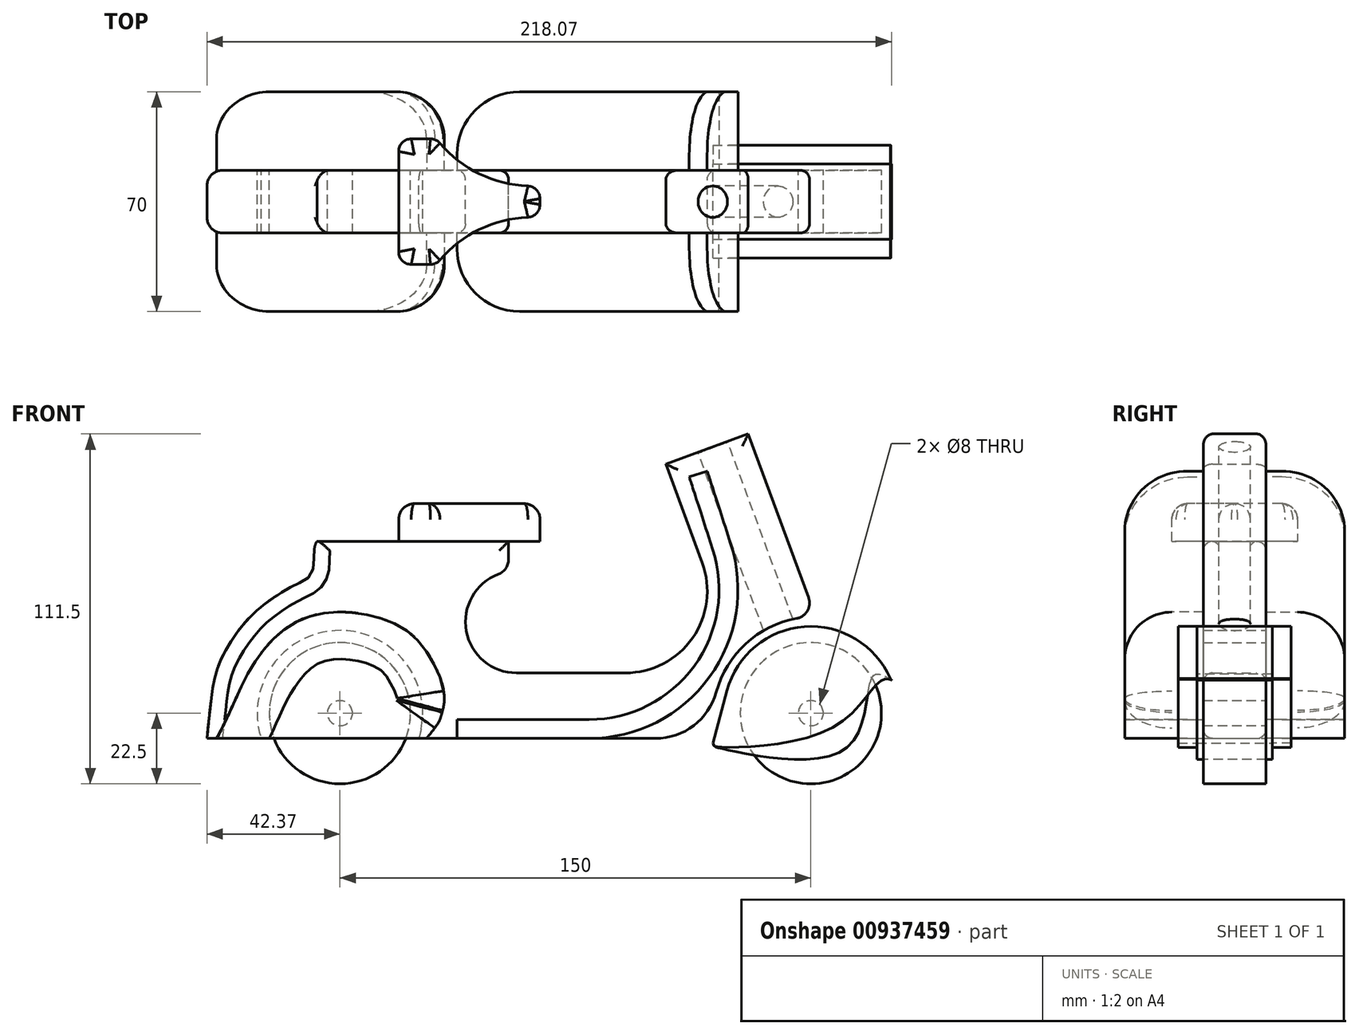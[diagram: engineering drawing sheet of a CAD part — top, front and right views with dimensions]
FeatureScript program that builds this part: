
annotation { "Feature Type Name" : "Feature", "Feature Type Description" : "" }
export const myFeature = defineFeature(function(context is Context, id is Id, definition is map)
    precondition{}
    {
        {
            var Q0;
            Q0=qCreatedBy(makeId("Front.planeOp"),FACE);
            var sketch = newSketch(context, id + "F0", { "sketchPlane" : qUnion([Q0])});
            skCircle(sketch, "E0", {"center": v(0, 0) * mm, "radius": 4 * mm, "construction": true});
            skCircle(sketch, "E1", {"center": v(0, 0) * mm, "radius": 22.5 * mm, "construction": true});
            skCircle(sketch, "E2", {"center": v(-150, 0) * mm, "radius": 4 * mm, "construction": true});
            skCircle(sketch, "E3", {"center": v(-150, 0) * mm, "radius": 22.5 * mm, "construction": true});
            skArc(sketch, "E4", {"start": v(1.52, 30.72) * mm, "mid": v(-23.75, 18.96) * mm, "end": v(-30.7, -8.03) * mm});
            skLineSegment(sketch, "E5", {"start": v(0, 0) * mm, "end": v(-39.23, 106.54) * mm, "construction": true});
            skArc(sketch, "E6", {"start": v(-124.9, -8.03) * mm, "mid": v(-150, 26.35) * mm, "end": v(-175.1, -8.03) * mm});
            skLineSegment(sketch, "E7", {"start": v(-30.7, -8.03) * mm, "end": v(-124.9, -8.03) * mm});
            skFitSpline(sketch, "E8", {"points": [v(-192.37, -8.03) * mm, v(-189.97, 10.9) * mm, v(-185.76, 21.1) * mm, v(-177.35, 31.92) * mm, v(-164.13, 40.93) * mm, v(-158.73, 45.14) * mm, v(-157.32, 54.76) * mm], "startDerivative": vector(9.9, 79.49) * mm, "endDerivative": vector(32.15, 42.3) * mm});
            skLineSegment(sketch, "E9", {"start": v(-157.32, 54.76) * mm, "end": v(-96.28, 54.76) * mm});
            skLineSegment(sketch, "E10", {"start": v(-96.28, 54.76) * mm, "end": v(-96.28, 45.15) * mm});
            skArc(sketch, "E11", {"start": v(-96.28, 45.15) * mm, "mid": v(-109.96, 27.81) * mm, "end": v(-93.75, 12.82) * mm});
            skLineSegment(sketch, "E12", {"start": v(-93.75, 12.82) * mm, "end": v(-59.07, 12.82) * mm});
            skArc(sketch, "E13", {"start": v(-59.07, 12.82) * mm, "mid": v(-37.68, 23.98) * mm, "end": v(-34.6, 47.9) * mm});
            skLineSegment(sketch, "E14", {"start": v(-34.6, 47.9) * mm, "end": v(-46.17, 79.34) * mm});
            skLineSegment(sketch, "E15", {"start": v(-46.17, 79.34) * mm, "end": v(-19.94, 89) * mm});
            skLineSegment(sketch, "E16", {"start": v(-19.94, 89) * mm, "end": v(1.52, 30.72) * mm});
            skLineSegment(sketch, "E17.trimOffspring", {"start": v(-175.1, -8.03) * mm, "end": v(-192.37, -8.03) * mm});
            skSolve(sketch);
        }
        {
            var Q0;
            Q0=makeQuery(id+"F0.imprint","IMPRINT",FACE,{"disambiguationData":[TD([[makeQuery(id+"F0.imprint","IMPRINT",EDGE,{"derivedFrom":sQuery(id+"F0.wireOp",EDGE,"E4")}),-1.0]])]});
            var Q1;
            Q1=sQuery(id+"F0.wireOp",EDGE,"E3");
            var Q2;
            Q2=sQuery(id+"F0.wireOp",EDGE,"E2");
            var Q3;
            Q3=sQuery(id+"F0.wireOp",EDGE,"E1");
            var Q4;
            Q4=sQuery(id+"F0.wireOp",EDGE,"E0");
            extrude(context, id + "F1", {"entities" : qUnion([Q0]), "surfaceEntities" : qUnion([Q1, Q2, Q3, Q4]), "depth" : 10 * mm, "offsetDistance" : 25 * mm, "hasSecondDirection" : true, "secondDirectionOppositeDirection" : true, "secondDirectionDepth" : 10 * mm});
        }
        {
            var Q0;
            Q0=makeQuery(id+"F1.opExtrude","SWEPT_FACE",FACE,{"disambiguationData":[OSD([sQuery(id+"F0.wireOp",EDGE,"E15")])]});
            var sketch = newSketch(context, id + "F2", { "sketchPlane" : qUnion([Q0])});
            skCircle(sketch, "E18", {"center": v(0, 0) * mm, "radius": 5 * mm});
            skSolve(sketch);
        }
        {
            var Q0;
            Q0 = qSketchRegion(id + "F2", true);
            extrude(context, id + "F3", {"entities" : qUnion([Q0]), "operationType" : NewBodyOperationType.REMOVE, "endBound" : BoundingType.THROUGH_ALL, "oppositeDirection" : true, "depth" : 25 * mm, "offsetDistance" : 25 * mm});
        }
        {
            var Q0;
            Q0=makeQuery(id+"F1.opExtrude","SWEPT_EDGE",EDGE,{"disambiguationData":[OSD([sQuery(id+"F0.wireOp",EDGE,"E4"),sQuery(id+"F0.wireOp",EDGE,"E16")])]});
            var Q1;
            Q1=makeQuery(id+"F1.opExtrude","SWEPT_EDGE",EDGE,{"disambiguationData":[OSD([sQuery(id+"F0.wireOp",EDGE,"E10"),sQuery(id+"F0.wireOp",EDGE,"E11")])]});
            fillet(context, id + "F4", {"entities" : qUnion([Q0, Q1]), "radius" : 5 * mm, "tangentPropagation" : true, "allowEdgeOverflow" : false});
        }
        {
            var Q0;
            Q0=makeQuery(id+"F1.opExtrude","SWEPT_EDGE",EDGE,{"disambiguationData":[OSD([sQuery(id+"F0.wireOp",EDGE,"E4"),sQuery(id+"F0.wireOp",EDGE,"E7")])]});
            fillet(context, id + "F5", {"entities" : qUnion([Q0]), "radius" : 20 * mm, "tangentPropagation" : true, "allowEdgeOverflow" : false});
        }
        {
            var Q0;
            Q0=makeQuery(id+"F1.opExtrude","CAP_EDGE",EDGE,{"disambiguationData":[OSD([sQuery(id+"F0.wireOp",EDGE,"E9")])],"isStart":true});
            var Q1;
            {var subQ0=sQuery(id+"F0.wireOp",EDGE,"E11");var subQ1=sQuery(id+"F0.wireOp",EDGE,"E10");Q1=makeQuery(id+"F4.opFillet","BLEND_EDGE",EDGE,{"blendedFrom":[makeQuery(id+"F1.opExtrude","SWEPT_EDGE",EDGE,{"disambiguationData":[OSD([subQ1,subQ0])]}),makeQuery(id+"F1.opExtrude","CAP_FACE",FACE,{"disambiguationData":[OSD([sQuery(id+"F0.wireOp",EDGE,"E4"),sQuery(id+"F0.wireOp",EDGE,"E6"),sQuery(id+"F0.wireOp",EDGE,"E7"),sQuery(id+"F0.wireOp",EDGE,"E8"),sQuery(id+"F0.wireOp",EDGE,"E9"),subQ1,subQ0,sQuery(id+"F0.wireOp",EDGE,"E12"),sQuery(id+"F0.wireOp",EDGE,"E13"),sQuery(id+"F0.wireOp",EDGE,"E14"),sQuery(id+"F0.wireOp",EDGE,"E15"),sQuery(id+"F0.wireOp",EDGE,"E16"),sQuery(id+"F0.wireOp",EDGE,"E17.trimOffspring")])],"isStart":true})],"blendedInto":[makeQuery(id+"F1.opExtrude","CAP_FACE",FACE,{"disambiguationData":[OSD([sQuery(id+"F0.wireOp",EDGE,"E4"),sQuery(id+"F0.wireOp",EDGE,"E6"),sQuery(id+"F0.wireOp",EDGE,"E7"),sQuery(id+"F0.wireOp",EDGE,"E8"),sQuery(id+"F0.wireOp",EDGE,"E9"),subQ1,subQ0,sQuery(id+"F0.wireOp",EDGE,"E12"),sQuery(id+"F0.wireOp",EDGE,"E13"),sQuery(id+"F0.wireOp",EDGE,"E14"),sQuery(id+"F0.wireOp",EDGE,"E15"),sQuery(id+"F0.wireOp",EDGE,"E16"),sQuery(id+"F0.wireOp",EDGE,"E17.trimOffspring")])],"isStart":true})]});}
            var Q2;
            Q2=makeQuery(id+"F1.opExtrude","CAP_EDGE",EDGE,{"disambiguationData":[OSD([sQuery(id+"F0.wireOp",EDGE,"E12")])],"isStart":true});
            var Q3;
            Q3=makeQuery(id+"F1.opExtrude","CAP_EDGE",EDGE,{"disambiguationData":[OSD([sQuery(id+"F0.wireOp",EDGE,"E13")])],"isStart":true});
            var Q4;
            Q4=makeQuery(id+"F1.opExtrude","CAP_EDGE",EDGE,{"disambiguationData":[OSD([sQuery(id+"F0.wireOp",EDGE,"E15")])],"isStart":true});
            var Q5;
            Q5=makeQuery(id+"F1.opExtrude","CAP_EDGE",EDGE,{"disambiguationData":[OSD([sQuery(id+"F0.wireOp",EDGE,"E16")])],"isStart":true});
            var Q6;
            Q6=makeQuery(id+"F1.opExtrude","CAP_EDGE",EDGE,{"disambiguationData":[OSD([sQuery(id+"F0.wireOp",EDGE,"E16")])],"isStart":false});
            var Q7;
            Q7=makeQuery(id+"F1.opExtrude","CAP_EDGE",EDGE,{"disambiguationData":[OSD([sQuery(id+"F0.wireOp",EDGE,"E15")])],"isStart":false});
            var Q8;
            Q8=makeQuery(id+"F1.opExtrude","CAP_EDGE",EDGE,{"disambiguationData":[OSD([sQuery(id+"F0.wireOp",EDGE,"E14")])],"isStart":false});
            var Q9;
            Q9=makeQuery(id+"F1.opExtrude","CAP_EDGE",EDGE,{"disambiguationData":[OSD([sQuery(id+"F0.wireOp",EDGE,"E13")])],"isStart":false});
            var Q10;
            Q10=makeQuery(id+"F1.opExtrude","CAP_EDGE",EDGE,{"disambiguationData":[OSD([sQuery(id+"F0.wireOp",EDGE,"E12")])],"isStart":false});
            var Q11;
            Q11=makeQuery(id+"F1.opExtrude","CAP_EDGE",EDGE,{"disambiguationData":[OSD([sQuery(id+"F0.wireOp",EDGE,"E11")])],"isStart":false});
            var Q12;
            {var subQ0=sQuery(id+"F0.wireOp",EDGE,"E11");var subQ1=sQuery(id+"F0.wireOp",EDGE,"E10");Q12=makeQuery(id+"F4.opFillet","BLEND_EDGE",EDGE,{"blendedFrom":[makeQuery(id+"F1.opExtrude","SWEPT_EDGE",EDGE,{"disambiguationData":[OSD([subQ1,subQ0])]}),makeQuery(id+"F1.opExtrude","CAP_FACE",FACE,{"disambiguationData":[OSD([sQuery(id+"F0.wireOp",EDGE,"E4"),sQuery(id+"F0.wireOp",EDGE,"E6"),sQuery(id+"F0.wireOp",EDGE,"E7"),sQuery(id+"F0.wireOp",EDGE,"E8"),sQuery(id+"F0.wireOp",EDGE,"E9"),subQ1,subQ0,sQuery(id+"F0.wireOp",EDGE,"E12"),sQuery(id+"F0.wireOp",EDGE,"E13"),sQuery(id+"F0.wireOp",EDGE,"E14"),sQuery(id+"F0.wireOp",EDGE,"E15"),sQuery(id+"F0.wireOp",EDGE,"E16"),sQuery(id+"F0.wireOp",EDGE,"E17.trimOffspring")])],"isStart":false})],"blendedInto":[makeQuery(id+"F1.opExtrude","CAP_FACE",FACE,{"disambiguationData":[OSD([sQuery(id+"F0.wireOp",EDGE,"E4"),sQuery(id+"F0.wireOp",EDGE,"E6"),sQuery(id+"F0.wireOp",EDGE,"E7"),sQuery(id+"F0.wireOp",EDGE,"E8"),sQuery(id+"F0.wireOp",EDGE,"E9"),subQ1,subQ0,sQuery(id+"F0.wireOp",EDGE,"E12"),sQuery(id+"F0.wireOp",EDGE,"E13"),sQuery(id+"F0.wireOp",EDGE,"E14"),sQuery(id+"F0.wireOp",EDGE,"E15"),sQuery(id+"F0.wireOp",EDGE,"E16"),sQuery(id+"F0.wireOp",EDGE,"E17.trimOffspring")])],"isStart":false})]});}
            var Q13;
            Q13=makeQuery(id+"F1.opExtrude","CAP_EDGE",EDGE,{"disambiguationData":[OSD([sQuery(id+"F0.wireOp",EDGE,"E9")])],"isStart":false});
            var Q14;
            Q14=makeQuery(id+"F1.opExtrude","CAP_EDGE",EDGE,{"disambiguationData":[OSD([sQuery(id+"F0.wireOp",EDGE,"E14")])],"isStart":true});
            var Q15;
            Q15=makeQuery(id+"F1.opExtrude","CAP_EDGE",EDGE,{"disambiguationData":[OSD([sQuery(id+"F0.wireOp",EDGE,"E11")])],"isStart":true});
            var Q16;
            Q16=makeQuery(id+"F1.opExtrude","CAP_EDGE",EDGE,{"disambiguationData":[OSD([sQuery(id+"F0.wireOp",EDGE,"E10")])],"isStart":false});
            var Q17;
            Q17=makeQuery(id+"F1.opExtrude","CAP_EDGE",EDGE,{"disambiguationData":[OSD([sQuery(id+"F0.wireOp",EDGE,"E10")])],"isStart":true});
            fillet(context, id + "F6", {"entities" : qUnion([Q0, Q1, Q2, Q3, Q4, Q5, Q6, Q7, Q8, Q9, Q10, Q11, Q12, Q13, Q14, Q15, Q16, Q17]), "radius" : 3 * mm, "tangentPropagation" : true, "allowEdgeOverflow" : false});
        }
        {
            var Q0;
            Q0=qCreatedBy(makeId("Front.planeOp"),FACE);
            var sketch = newSketch(context, id + "F7", { "sketchPlane" : qUnion([Q0])});
            skCircle(sketch, "E19.0", {"center": v(-150, 0) * mm, "radius": 22.5 * mm});
            skCircle(sketch, "E20.0", {"center": v(-150, 0) * mm, "radius": 4 * mm});
            skCircle(sketch, "E21.0", {"center": v(0, 0) * mm, "radius": 22.5 * mm});
            skCircle(sketch, "E22.0", {"center": v(0, 0) * mm, "radius": 4 * mm});
            skSolve(sketch);
        }
        {
            var Q0;
            Q0 = qSketchRegion(id + "F7", true);
            extrude(context, id + "F8", {"entities" : qUnion([Q0]), "depth" : 10 * mm, "offsetDistance" : 25 * mm, "hasSecondDirection" : true, "secondDirectionOppositeDirection" : true, "secondDirectionDepth" : 10 * mm});
        }
        {
            var Q0;
            Q0=makeQuery(id+"F1.opExtrude","CAP_FACE",FACE,{"disambiguationData":[OSD([sQuery(id+"F0.wireOp",EDGE,"E4"),sQuery(id+"F0.wireOp",EDGE,"E6"),sQuery(id+"F0.wireOp",EDGE,"E7"),sQuery(id+"F0.wireOp",EDGE,"E8"),sQuery(id+"F0.wireOp",EDGE,"E9"),sQuery(id+"F0.wireOp",EDGE,"E10"),sQuery(id+"F0.wireOp",EDGE,"E11"),sQuery(id+"F0.wireOp",EDGE,"E12"),sQuery(id+"F0.wireOp",EDGE,"E13"),sQuery(id+"F0.wireOp",EDGE,"E14"),sQuery(id+"F0.wireOp",EDGE,"E15"),sQuery(id+"F0.wireOp",EDGE,"E16"),sQuery(id+"F0.wireOp",EDGE,"E17.trimOffspring")])],"isStart":false});
            var sketch = newSketch(context, id + "F9", { "sketchPlane" : qUnion([Q0])});
            skLineSegment(sketch, "E23", {"start": v(-189.27, -8.03) * mm, "end": v(-122.4, -8.03) * mm});
            skFitSpline(sketch, "E24", {"points": [v(-122.4, -8.03) * mm, v(-118.5, -2.76) * mm, v(-117.52, 0) * mm, v(-116.74, 4.25) * mm, v(-117.77, 10.42) * mm, v(-120.05, 15.55) * mm, v(-126.29, 24.31) * mm, v(-138.75, 30.74) * mm, v(-152.78, 32.1) * mm, v(-165.83, 28.01) * mm, v(-178.3, 14.38) * mm, v(-189.27, -8.03) * mm], "startDerivative": vector(67.66, 86) * mm, "endDerivative": vector(-92.65, -168.88) * mm});
            skSolve(sketch);
        }
        {
            var Q0;
            Q0 = qSketchRegion(id + "F9", true);
            extrude(context, id + "F10", {"entities" : qUnion([Q0]), "depth" : 25 * mm, "offsetDistance" : 25 * mm});
        }
        {
            var Q0;
            Q0=makeQuery(id+"F10.opExtrude","CAP_EDGE",EDGE,{"disambiguationData":[OSD([sQuery(id+"F9.wireOp",EDGE,"E24")])],"isStart":false});
            fillet(context, id + "F11", {"entities" : qUnion([Q0]), "radius" : 15 * mm, "tangentPropagation" : true, "allowEdgeOverflow" : false});
        }
        {
            var Q0;
            Q0=makeQuery(id+"F10.opExtrude","SWEPT_BODY",BODY,{"disambiguationData":[OSD([sQuery(id+"F9.wireOp",EDGE,"E23"),sQuery(id+"F9.wireOp",EDGE,"E24")])]});
            var Q1;
            Q1=qCreatedBy(makeId("Front.planeOp"),FACE);
            mirror(context, id + "F12", {"entities" : qUnion([Q0]), "mirrorPlane" : qUnion([Q1])});
        }
        {
            var Q0;
            Q0=makeQuery(id+"F1.opExtrude","SWEPT_FACE",FACE,{"disambiguationData":[OSD([sQuery(id+"F0.wireOp",EDGE,"E9")])]});
            var sketch = newSketch(context, id + "F13", { "sketchPlane" : qUnion([Q0])});
            skLineSegment(sketch, "E25", {"start": v(-131.28, 0) * mm, "end": v(-131.28, -20) * mm});
            skLineSegment(sketch, "E26", {"start": v(-131.28, -20) * mm, "end": v(-119.28, -20) * mm});
            skLineSegment(sketch, "E27", {"start": v(-86.28, -5) * mm, "end": v(-86.28, 0) * mm});
            skLineSegment(sketch, "E28", {"start": v(-101.42, 0) * mm, "end": v(-376.72, 0) * mm, "construction": true});
            skLineSegment(sketch, "E29.MirrorCS", {"start": v(-86.28, 5) * mm, "end": v(-86.28, 0) * mm});
            skLineSegment(sketch, "E30.MirrorCS", {"start": v(-131.28, 0) * mm, "end": v(-131.28, 20) * mm});
            skLineSegment(sketch, "E31.MirrorCS", {"start": v(-131.28, 20) * mm, "end": v(-119.28, 20) * mm});
            skArc(sketch, "E32", {"start": v(-86.28, -5) * mm, "mid": v(-104.63, -8.43) * mm, "end": v(-119.28, -20) * mm});
            skArc(sketch, "E33.MirrorCS", {"start": v(-86.28, 5) * mm, "mid": v(-104.63, 8.43) * mm, "end": v(-119.28, 20) * mm});
            skSolve(sketch);
        }
        {
            var Q0;
            Q0 = qSketchRegion(id + "F13", true);
            extrude(context, id + "F14", {"entities" : qUnion([Q0]), "depth" : 12 * mm, "offsetDistance" : 25 * mm});
        }
        {
            var Q0;
            Q0=makeQuery(id+"F14.opExtrude","SWEPT_EDGE",EDGE,{"disambiguationData":[OSD([sQuery(id+"F13.wireOp",EDGE,"E25"),sQuery(id+"F13.wireOp",EDGE,"E26")])]});
            var Q1;
            Q1=makeQuery(id+"F14.opExtrude","SWEPT_EDGE",EDGE,{"disambiguationData":[OSD([sQuery(id+"F13.wireOp",EDGE,"E26"),sQuery(id+"F13.wireOp",EDGE,"D86m4NS1-QapF-7dMu-qflW-tjYcYlbxfgkB")])]});
            var Q2;
            Q2=makeQuery(id+"F14.opExtrude","SWEPT_EDGE",EDGE,{"disambiguationData":[OSD([sQuery(id+"F13.wireOp",EDGE,"D86m4NS1-QapF-7dMu-qflW-tjYcYlbxfgkB"),sQuery(id+"F13.wireOp",EDGE,"E27")])]});
            var Q3;
            Q3=makeQuery(id+"F14.opExtrude","SWEPT_EDGE",EDGE,{"disambiguationData":[OSD([sQuery(id+"F13.wireOp",EDGE,"E29.MirrorCS"),sQuery(id+"F13.wireOp",EDGE,"5b569bc2-48fd-4aba-aae6-d2839cf5999e2.MirrorCS")])]});
            var Q4;
            Q4=makeQuery(id+"F14.opExtrude","SWEPT_EDGE",EDGE,{"disambiguationData":[OSD([sQuery(id+"F13.wireOp",EDGE,"E30.MirrorCS"),sQuery(id+"F13.wireOp",EDGE,"E31.MirrorCS")])]});
            var Q5;
            Q5=makeQuery(id+"F14.opExtrude","SWEPT_EDGE",EDGE,{"disambiguationData":[OSD([sQuery(id+"F13.wireOp",EDGE,"5b569bc2-48fd-4aba-aae6-d2839cf5999e2.MirrorCS"),sQuery(id+"F13.wireOp",EDGE,"E31.MirrorCS")])]});
            fillet(context, id + "F15", {"entities" : qUnion([Q0, Q1, Q2, Q3, Q4, Q5]), "radius" : 4 * mm, "tangentPropagation" : true, "allowEdgeOverflow" : false});
        }
        {
            var Q0;
            Q0=makeQuery(id+"F14.opExtrude","CAP_FACE",FACE,{"disambiguationData":[OSD([sQuery(id+"F13.wireOp",EDGE,"E25"),sQuery(id+"F13.wireOp",EDGE,"E26"),sQuery(id+"F13.wireOp",EDGE,"E27"),sQuery(id+"F13.wireOp",EDGE,"E29.MirrorCS"),sQuery(id+"F13.wireOp",EDGE,"E30.MirrorCS"),sQuery(id+"F13.wireOp",EDGE,"E31.MirrorCS"),sQuery(id+"F13.wireOp",EDGE,"E32"),sQuery(id+"F13.wireOp",EDGE,"E33.MirrorCS")])],"isStart":false});
            fillet(context, id + "F16", {"entities" : qUnion([Q0]), "radius" : 5 * mm, "tangentPropagation" : true, "allowEdgeOverflow" : false});
        }
        {
            var Q0;
            Q0=makeQuery(id+"F1.opExtrude","CAP_EDGE",EDGE,{"disambiguationData":[OSD([sQuery(id+"F0.wireOp",EDGE,"E8")])],"isStart":true});
            var Q1;
            Q1=makeQuery(id+"F1.opExtrude","CAP_EDGE",EDGE,{"disambiguationData":[OSD([sQuery(id+"F0.wireOp",EDGE,"E8")])],"isStart":false});
            fillet(context, id + "F17", {"entities" : qUnion([Q0, Q1]), "radius" : 5 * mm, "allowEdgeOverflow" : false});
        }
        {
            var Q0;
            Q0=makeQuery(id+"F1.opExtrude","CAP_FACE",FACE,{"disambiguationData":[OSD([sQuery(id+"F0.wireOp",EDGE,"E4"),sQuery(id+"F0.wireOp",EDGE,"E6"),sQuery(id+"F0.wireOp",EDGE,"E7"),sQuery(id+"F0.wireOp",EDGE,"E8"),sQuery(id+"F0.wireOp",EDGE,"E9"),sQuery(id+"F0.wireOp",EDGE,"E10"),sQuery(id+"F0.wireOp",EDGE,"E11"),sQuery(id+"F0.wireOp",EDGE,"E12"),sQuery(id+"F0.wireOp",EDGE,"E13"),sQuery(id+"F0.wireOp",EDGE,"E14"),sQuery(id+"F0.wireOp",EDGE,"E15"),sQuery(id+"F0.wireOp",EDGE,"E16"),sQuery(id+"F0.wireOp",EDGE,"E17.trimOffspring")])],"isStart":false});
            var sketch = newSketch(context, id + "F18", { "sketchPlane" : qUnion([Q0])});
            skArc(sketch, "E34", {"start": v(-70.65, -2.03) * mm, "mid": v(-37.15, 15.02) * mm, "end": v(-31.24, 52.14) * mm});
            skLineSegment(sketch, "E35", {"start": v(-112.73, -2.03) * mm, "end": v(-70.65, -2.03) * mm});
            skLineSegment(sketch, "E36", {"start": v(-31.24, 52.14) * mm, "end": v(-38.72, 75.28) * mm});
            skLineSegment(sketch, "E37.0", {"start": v(-25.53, 53.99) * mm, "end": v(-33.01, 77.13) * mm});
            skArc(sketch, "E37.1", {"start": v(-70.65, -8.03) * mm, "mid": v(-32.3, 11.5) * mm, "end": v(-25.53, 53.99) * mm});
            skLineSegment(sketch, "E37.2", {"start": v(-112.73, -8.03) * mm, "end": v(-70.65, -8.03) * mm});
            skLineSegment(sketch, "E38", {"start": v(-112.73, -8.03) * mm, "end": v(-112.73, -2.03) * mm});
            skLineSegment(sketch, "E39", {"start": v(-38.72, 75.28) * mm, "end": v(-33.01, 77.13) * mm});
            skSolve(sketch);
        }
        {
            var Q0;
            Q0 = qSketchRegion(id + "F18", true);
            extrude(context, id + "F19", {"entities" : qUnion([Q0]), "depth" : 25 * mm, "offsetDistance" : 25 * mm});
        }
        {
            var Q0;
            Q0=makeQuery(id+"F19.opExtrude","CAP_EDGE",EDGE,{"disambiguationData":[OSD([sQuery(id+"F18.wireOp",EDGE,"E38")])],"isStart":false});
            var Q1;
            Q1=makeQuery(id+"F19.opExtrude","CAP_EDGE",EDGE,{"disambiguationData":[OSD([sQuery(id+"F18.wireOp",EDGE,"E39")])],"isStart":false});
            fillet(context, id + "F20", {"entities" : qUnion([Q0, Q1]), "radius" : 20 * mm, "tangentPropagation" : true, "allowEdgeOverflow" : false});
        }
        {
            var Q0;
            Q0=makeQuery(id+"F19.opExtrude","SWEPT_BODY",BODY,{"disambiguationData":[OSD([sQuery(id+"F18.wireOp",EDGE,"E34"),sQuery(id+"F18.wireOp",EDGE,"E35"),sQuery(id+"F18.wireOp",EDGE,"E36"),sQuery(id+"F18.wireOp",EDGE,"E37.0"),sQuery(id+"F18.wireOp",EDGE,"E37.1"),sQuery(id+"F18.wireOp",EDGE,"E37.2"),sQuery(id+"F18.wireOp",EDGE,"E38"),sQuery(id+"F18.wireOp",EDGE,"E39")])]});
            var Q1;
            Q1=qCreatedBy(makeId("Front.planeOp"),FACE);
            mirror(context, id + "F21", {"entities" : qUnion([Q0]), "mirrorPlane" : qUnion([Q1])});
        }
        {
            var Q0;
            Q0=qCreatedBy(makeId("Front.planeOp"),FACE);
            cPlane(context, id + "F22", {"entities" : qUnion([Q0]), "cplaneType" : CPlaneType.OFFSET, "offset" : 12 * mm, "width" : 150 * mm, "height" : 150 * mm});
        }
        {
            var Q0;
            Q0=qCreatedBy(id+"F22.planeOp",FACE);
            var sketch = newSketch(context, id + "F23", { "sketchPlane" : qUnion([Q0])});
            skArc(sketch, "E40", {"start": v(25.43, 10.83) * mm, "mid": v(-1.91, 27.57) * mm, "end": v(-26.68, 7.22) * mm});
            skFitSpline(sketch, "E41", {"points": [v(-31.22, -9.58) * mm, v(-30.67, -10.38) * mm, v(-29.18, -10.8) * mm, v(7.62, -4.2) * mm, v(23, 10.71) * mm, v(25.43, 10.83) * mm, v(25.31, 11.09) * mm], "startDerivative": vector(8.04, -13.7) * mm, "endDerivative": vector(-6.42, 9.22) * mm});
            skLineSegment(sketch, "E42", {"start": v(-31.22, -9.58) * mm, "end": v(-26.68, 7.22) * mm});
            skSolve(sketch);
        }
        {
            var Q0;
            Q0 = qSketchRegion(id + "F23", true);
            extrude(context, id + "F24", {"entities" : qUnion([Q0]), "depth" : 6 * mm, "offsetDistance" : 25 * mm});
        }
        {
            var Q0;
            Q0=makeQuery(id+"F24.opExtrude","SWEPT_BODY",BODY,{"disambiguationData":[OSD([sQuery(id+"F23.wireOp",EDGE,"E40"),sQuery(id+"F23.wireOp",EDGE,"E41"),sQuery(id+"F23.wireOp",EDGE,"E42")])]});
            var Q1;
            Q1=qCreatedBy(makeId("Front.planeOp"),FACE);
            mirror(context, id + "F25", {"entities" : qUnion([Q0]), "mirrorPlane" : qUnion([Q1])});
        }
        {
            var Q0;
            Q0=makeQuery(id+"F25.opPattern","COPY",FACE,{"derivedFrom":makeQuery(id+"F24.opExtrude","CAP_FACE",FACE,{"disambiguationData":[OSD([sQuery(id+"F23.wireOp",EDGE,"E40"),sQuery(id+"F23.wireOp",EDGE,"E41"),sQuery(id+"F23.wireOp",EDGE,"E42")])],"isStart":true}),"instanceName":"1"});
            var sketch = newSketch(context, id + "F26", { "sketchPlane" : qUnion([Q0])});
            skArc(sketch, "E43.0", {"start": v(25.31, 11.09) * mm, "mid": v(-2.05, 27.56) * mm, "end": v(-26.68, 7.22) * mm});
            skLineSegment(sketch, "E44.0", {"start": v(-31.22, -9.58) * mm, "end": v(-26.68, 7.22) * mm});
            skLineSegment(sketch, "E45.0", {"start": v(-26.4, -10.88) * mm, "end": v(-21.85, 5.91) * mm});
            skArc(sketch, "E45.1", {"start": v(20.76, 9.01) * mm, "mid": v(-1.64, 22.58) * mm, "end": v(-21.85, 5.91) * mm});
            skFitSpline(sketch, "E46.0", {"points": [v(-31.22, -9.58) * mm, v(-31.05, -9.88) * mm, v(-30.65, -10.56) * mm, v(-28.71, -11.18) * mm, v(11.87, -10.62) * mm, v(20.7, 12.4) * mm, v(25.7, 10.56) * mm, v(25.39, 10.98) * mm, v(25.31, 11.09) * mm]});
            skFitSpline(sketch, "E47.trimOffspring", {"points": [v(-31.22, -9.58) * mm, v(-31.05, -9.88) * mm, v(-30.65, -10.56) * mm, v(-28.71, -11.18) * mm, v(11.87, -10.62) * mm, v(20.7, 12.4) * mm, v(25.7, 10.56) * mm, v(25.39, 10.98) * mm, v(25.31, 11.09) * mm]});
            skSolve(sketch);
        }
        {
            var Q0;
            Q0 = qSketchRegion(id + "F26", true);
            var Q1;
            Q1=makeQuery(id+"F24.opExtrude","CAP_FACE",FACE,{"disambiguationData":[OSD([sQuery(id+"F23.wireOp",EDGE,"E40"),sQuery(id+"F23.wireOp",EDGE,"E41"),sQuery(id+"F23.wireOp",EDGE,"E42")])],"isStart":true});
            extrude(context, id + "F27", {"entities" : qUnion([Q0]), "endBound" : BoundingType.UP_TO_SURFACE, "depth" : 25 * mm, "endBoundEntityFace" : qUnion([Q1]), "offsetDistance" : 25 * mm});
        }
    });
